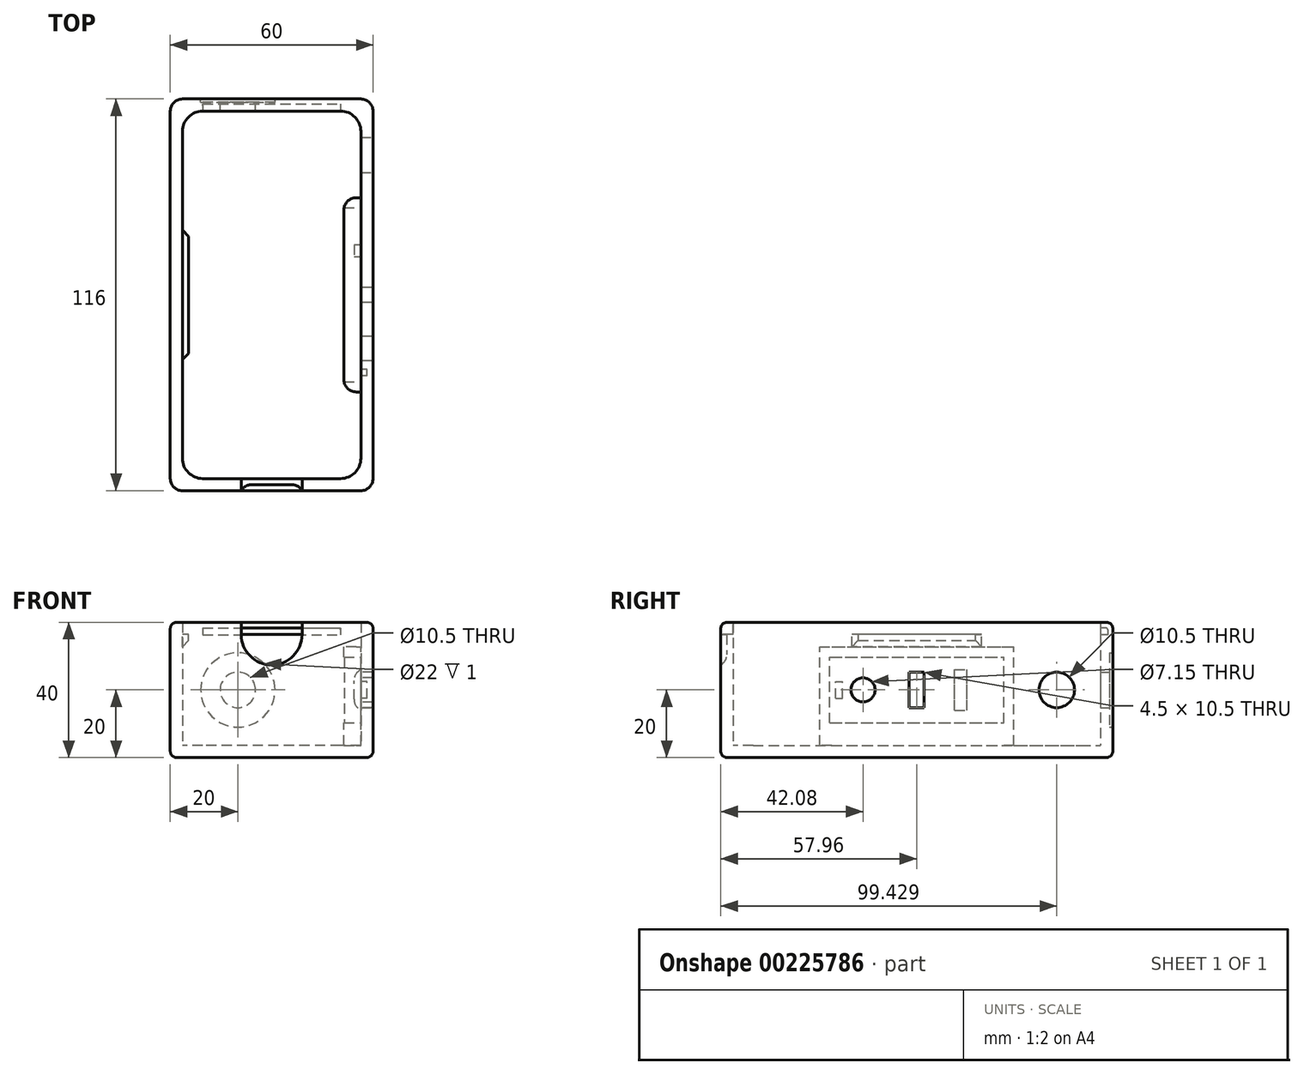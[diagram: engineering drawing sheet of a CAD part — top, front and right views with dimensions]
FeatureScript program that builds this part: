
annotation { "Feature Type Name" : "Feature", "Feature Type Description" : "" }
export const myFeature = defineFeature(function(context is Context, id is Id, definition is map)
    precondition{}
    {
        {
            assignVariable(context, id + "F0", {"name" : "O", "anyValue" : 3.6});
        }
        {
            assignVariable(context, id + "F1", {"name" : "H", "anyValue" : 40});
        }
        {
            var Q0;
            Q0=qCreatedBy(makeId("Top.planeOp"),FACE);
            var sketch = newSketch(context, id + "F2", { "sketchPlane" : qUnion([Q0])});
            skLineSegment(sketch, "E0.bottom", {"start": v(30, -58) * mm, "end": v(-30, -58) * mm});
            skLineSegment(sketch, "E0.top", {"start": v(30, 58) * mm, "end": v(-30, 58) * mm});
            skLineSegment(sketch, "E0.left", {"start": v(30, -58) * mm, "end": v(30, 58) * mm});
            skLineSegment(sketch, "E0.right", {"start": v(-30, -58) * mm, "end": v(-30, 58) * mm});
            skPoint(sketch, "E0.middle", {"position": v(0, 0) * mm});
            skLineSegment(sketch, "E1.0", {"start": v(26.4, 54.4) * mm, "end": v(-26.4, 54.4) * mm});
            skLineSegment(sketch, "E1.1", {"start": v(26.4, -54.4) * mm, "end": v(26.4, 54.4) * mm});
            skLineSegment(sketch, "E1.2", {"start": v(26.4, -54.4) * mm, "end": v(-26.4, -54.4) * mm});
            skLineSegment(sketch, "E1.3", {"start": v(-26.4, -54.4) * mm, "end": v(-26.4, 54.4) * mm});
            skSolve(sketch);
        }
        {
            var Q0;
            Q0=makeQuery(id+"F2.imprint","IMPRINT",FACE,{"disambiguationData":[TD([[makeQuery(id+"F2.imprint","IMPRINT",EDGE,{"derivedFrom":sQuery(id+"F2.wireOp",EDGE,"E0.bottom")}),-1.0]])]});
            extrude(context, id + "F3", {"entities" : qUnion([Q0]), "depth" : (getVariable(context, 'H')) * mm});
        }
        {
            var Q0;
            Q0=makeQuery(id+"F2.imprint","IMPRINT",FACE,{"disambiguationData":[TD([[makeQuery(id+"F2.imprint","IMPRINT",EDGE,{"derivedFrom":sQuery(id+"F2.wireOp",EDGE,"E1.0")}),1.0]])]});
            extrude(context, id + "F4", {"entities" : qUnion([Q0]), "operationType" : NewBodyOperationType.ADD, "depth" : (getVariable(context, 'O')) * mm});
        }
        {
            var Q0;
            Q0=makeQuery(id+"F3.opExtrude","SWEPT_FACE",FACE,{"disambiguationData":[OSD([sQuery(id+"F2.wireOp",EDGE,"E0.left")])]});
            var sketch = newSketch(context, id + "F5", { "sketchPlane" : qUnion([Q0])});
            skCircle(sketch, "E2", {"center": v(41.43, 20) * mm, "radius": 5.25 * mm});
            skSolve(sketch);
        }
        {
            var Q0;
            Q0=makeQuery(id+"F3.opExtrude","SWEPT_FACE",FACE,{"disambiguationData":[OSD([sQuery(id+"F2.wireOp",EDGE,"E0.top")])]});
            var sketch = newSketch(context, id + "F6", { "sketchPlane" : qUnion([Q0])});
            skCircle(sketch, "E3", {"center": v(10, 20) * mm, "radius": 5.25 * mm});
            skCircle(sketch, "E4", {"center": v(10, 20) * mm, "radius": 11 * mm});
            skSolve(sketch);
        }
        {
            var Q0;
            Q0=makeQuery(id+"F3.opExtrude","SWEPT_EDGE",EDGE,{"disambiguationData":[OSD([sQuery(id+"F2.wireOp",EDGE,"E0.top"),sQuery(id+"F2.wireOp",EDGE,"E0.left")])]});
            var Q1;
            Q1=makeQuery(id+"F3.opExtrude","SWEPT_EDGE",EDGE,{"disambiguationData":[OSD([sQuery(id+"F2.wireOp",EDGE,"E0.top"),sQuery(id+"F2.wireOp",EDGE,"E0.right")])]});
            var Q2;
            Q2=makeQuery(id+"F3.opExtrude","SWEPT_EDGE",EDGE,{"disambiguationData":[OSD([sQuery(id+"F2.wireOp",EDGE,"E0.bottom"),sQuery(id+"F2.wireOp",EDGE,"E0.right")])]});
            var Q3;
            Q3=makeQuery(id+"F3.opExtrude","SWEPT_EDGE",EDGE,{"disambiguationData":[OSD([sQuery(id+"F2.wireOp",EDGE,"E0.bottom"),sQuery(id+"F2.wireOp",EDGE,"E0.left")])]});
            fillet(context, id + "F7", {"entities" : qUnion([Q0, Q1, Q2, Q3]), "radius" : (getVariable(context, 'O')) * mm, "tangentPropagation" : true, "allowEdgeOverflow" : false});
        }
        {
            var Q0;
            Q0=makeQuery(id+"F3.opExtrude","SWEPT_EDGE",EDGE,{"disambiguationData":[OSD([sQuery(id+"F2.wireOp",EDGE,"E1.2"),sQuery(id+"F2.wireOp",EDGE,"E1.3")])]});
            var Q1;
            Q1=makeQuery(id+"F3.opExtrude","SWEPT_EDGE",EDGE,{"disambiguationData":[OSD([sQuery(id+"F2.wireOp",EDGE,"E1.1"),sQuery(id+"F2.wireOp",EDGE,"E1.2")])]});
            var Q2;
            Q2=makeQuery(id+"F3.opExtrude","SWEPT_EDGE",EDGE,{"disambiguationData":[OSD([sQuery(id+"F2.wireOp",EDGE,"E1.0"),sQuery(id+"F2.wireOp",EDGE,"E1.1")])]});
            var Q3;
            Q3=makeQuery(id+"F3.opExtrude","SWEPT_EDGE",EDGE,{"disambiguationData":[OSD([sQuery(id+"F2.wireOp",EDGE,"E1.0"),sQuery(id+"F2.wireOp",EDGE,"E1.3")])]});
            fillet(context, id + "F8", {"entities" : qUnion([Q0, Q1, Q2, Q3]), "radius" : (getVariable(context, 'O') * 1.67) * mm, "tangentPropagation" : true, "allowEdgeOverflow" : false});
        }
        {
            var Q0;
            Q0=makeQuery(id+"F6.imprint","IMPRINT",FACE,{"disambiguationData":[TD([[makeQuery(id+"F6.imprint","IMPRINT",EDGE,{"derivedFrom":sQuery(id+"F6.wireOp",EDGE,"E3")}),1.0]])]});
            extrude(context, id + "F9", {"entities" : qUnion([Q0]), "operationType" : NewBodyOperationType.REMOVE, "oppositeDirection" : true, "depth" : (getVariable(context, 'O')) * mm});
        }
        {
            var Q0;
            Q0=makeQuery(id+"F5.imprint","IMPRINT",FACE,{"disambiguationData":[TD([[makeQuery(id+"F5.imprint","IMPRINT",EDGE,{"derivedFrom":sQuery(id+"F5.wireOp",EDGE,"E2")}),1.0]])]});
            extrude(context, id + "F10", {"entities" : qUnion([Q0]), "operationType" : NewBodyOperationType.REMOVE, "oppositeDirection" : true, "depth" : (getVariable(context, 'O')) * mm});
        }
        {
            var Q0;
            Q0=makeQuery(id+"F3.opExtrude","SWEPT_FACE",FACE,{"disambiguationData":[OSD([sQuery(id+"F2.wireOp",EDGE,"E0.bottom")])]});
            var sketch = newSketch(context, id + "F11", { "sketchPlane" : qUnion([Q0])});
            skLineSegment(sketch, "E5.bottom", {"start": v(9, 36.4) * mm, "end": v(-9, 36.4) * mm});
            skLineSegment(sketch, "E5.top", {"start": v(9, 40) * mm, "end": v(-9, 40) * mm});
            skLineSegment(sketch, "E5.left", {"start": v(9, 36.4) * mm, "end": v(9, 40) * mm});
            skLineSegment(sketch, "E5.right", {"start": v(-9, 36.4) * mm, "end": v(-9, 40) * mm});
            skPoint(sketch, "E5.middle", {"position": v(0, 38.2) * mm});
            skPoint(sketch, "E5.middle.positionSnap0", {"position": v(0, 0) * mm});
            skPoint(sketch, "E5.centerSnap0", {"position": v(0, 0) * mm});
            skArc(sketch, "E6", {"start": v(-9, 36.4) * mm, "mid": v(0, 27.4) * mm, "end": v(9, 36.4) * mm});
            skSolve(sketch);
        }
        {
            var Q0;
            Q0=makeQuery(id+"F11.imprint","IMPRINT",FACE,{"disambiguationData":[TD([[makeQuery(id+"F11.imprint","IMPRINT",EDGE,{"derivedFrom":sQuery(id+"F11.wireOp",EDGE,"E5.bottom")}),-1.0]])]});
            extrude(context, id + "F12", {"entities" : qUnion([Q0]), "operationType" : NewBodyOperationType.REMOVE, "oppositeDirection" : true, "depth" : (getVariable(context, 'O')) * mm});
        }
        {
            var Q0;
            Q0=makeQuery(id+"F3.opExtrude","SWEPT_FACE",FACE,{"disambiguationData":[OSD([sQuery(id+"F2.wireOp",EDGE,"E1.0")])]});
            var sketch = newSketch(context, id + "F13", { "sketchPlane" : qUnion([Q0])});
            skLineSegment(sketch, "E7.bottom", {"start": v(-20.4, 38.3) * mm, "end": v(20.4, 38.3) * mm});
            skLineSegment(sketch, "E7.top", {"start": v(-20.4, 36.3) * mm, "end": v(20.4, 36.3) * mm});
            skLineSegment(sketch, "E7.left", {"start": v(-20.4, 38.3) * mm, "end": v(-20.4, 36.3) * mm});
            skLineSegment(sketch, "E7.right", {"start": v(20.4, 38.3) * mm, "end": v(20.4, 36.3) * mm});
            skSolve(sketch);
        }
        {
            var Q0;
            Q0=makeQuery(id+"F13.imprint","IMPRINT",FACE,{"disambiguationData":[TD([[makeQuery(id+"F13.imprint","IMPRINT",EDGE,{"derivedFrom":sQuery(id+"F13.wireOp",EDGE,"E7.bottom")}),-1.0]])]});
            extrude(context, id + "F14", {"entities" : qUnion([Q0]), "operationType" : NewBodyOperationType.REMOVE, "oppositeDirection" : true, "depth" : 2.1 * mm});
        }
        {
            var Q0;
            {var subQ0=sQuery(id+"F2.wireOp",EDGE,"E0.bottom");Q0=makeQuery(id+"F12.boolean.opBoolean","SPLIT",EDGE,{"disambiguationData":[TD([makeQuery(id+"F12.opExtrude","SWEPT_FACE",FACE,{"disambiguationData":[OSD([sQuery(id+"F11.wireOp",EDGE,"E5.left")])]})])],"derivedFrom":makeQuery(id+"F3.opExtrude","CAP_EDGE",EDGE,{"disambiguationData":[OSD([subQ0])],"isStart":false})});}
            var Q1;
            {var subQ0=sQuery(id+"F2.wireOp",EDGE,"E0.left");var subQ1=sQuery(id+"F2.wireOp",EDGE,"E0.bottom");Q1=makeQuery(id+"F7.opFillet","BLEND_EDGE",EDGE,{"blendedFrom":[makeQuery(id+"F3.opExtrude","SWEPT_EDGE",EDGE,{"disambiguationData":[OSD([subQ1,subQ0])]}),makeQuery(id+"F3.opExtrude","CAP_FACE",FACE,{"disambiguationData":[OSD([subQ1,sQuery(id+"F2.wireOp",EDGE,"E0.top"),subQ0,sQuery(id+"F2.wireOp",EDGE,"E0.right"),sQuery(id+"F2.wireOp",EDGE,"E1.0"),sQuery(id+"F2.wireOp",EDGE,"E1.1"),sQuery(id+"F2.wireOp",EDGE,"E1.2"),sQuery(id+"F2.wireOp",EDGE,"E1.3")])],"isStart":false})],"blendedInto":[makeQuery(id+"F3.opExtrude","CAP_FACE",FACE,{"disambiguationData":[OSD([subQ1,sQuery(id+"F2.wireOp",EDGE,"E0.top"),subQ0,sQuery(id+"F2.wireOp",EDGE,"E0.right"),sQuery(id+"F2.wireOp",EDGE,"E1.0"),sQuery(id+"F2.wireOp",EDGE,"E1.1"),sQuery(id+"F2.wireOp",EDGE,"E1.2"),sQuery(id+"F2.wireOp",EDGE,"E1.3")])],"isStart":false})]});}
            var Q2;
            Q2=makeQuery(id+"F3.opExtrude","CAP_EDGE",EDGE,{"disambiguationData":[OSD([sQuery(id+"F2.wireOp",EDGE,"E0.left")])],"isStart":false});
            var Q3;
            {var subQ0=sQuery(id+"F2.wireOp",EDGE,"E0.bottom");Q3=makeQuery(id+"F12.boolean.opBoolean","SPLIT",EDGE,{"disambiguationData":[TD([makeQuery(id+"F12.opExtrude","SWEPT_FACE",FACE,{"disambiguationData":[OSD([sQuery(id+"F11.wireOp",EDGE,"E5.right")])]})])],"derivedFrom":makeQuery(id+"F3.opExtrude","CAP_EDGE",EDGE,{"disambiguationData":[OSD([subQ0])],"isStart":false})});}
            var Q4;
            {var subQ0=sQuery(id+"F2.wireOp",EDGE,"E0.right");var subQ1=sQuery(id+"F2.wireOp",EDGE,"E0.bottom");Q4=makeQuery(id+"F7.opFillet","BLEND_EDGE",EDGE,{"blendedFrom":[makeQuery(id+"F3.opExtrude","SWEPT_EDGE",EDGE,{"disambiguationData":[OSD([subQ1,subQ0])]}),makeQuery(id+"F3.opExtrude","CAP_FACE",FACE,{"disambiguationData":[OSD([subQ1,sQuery(id+"F2.wireOp",EDGE,"E0.top"),sQuery(id+"F2.wireOp",EDGE,"E0.left"),subQ0,sQuery(id+"F2.wireOp",EDGE,"E1.0"),sQuery(id+"F2.wireOp",EDGE,"E1.1"),sQuery(id+"F2.wireOp",EDGE,"E1.2"),sQuery(id+"F2.wireOp",EDGE,"E1.3")])],"isStart":false})],"blendedInto":[makeQuery(id+"F3.opExtrude","CAP_FACE",FACE,{"disambiguationData":[OSD([subQ1,sQuery(id+"F2.wireOp",EDGE,"E0.top"),sQuery(id+"F2.wireOp",EDGE,"E0.left"),subQ0,sQuery(id+"F2.wireOp",EDGE,"E1.0"),sQuery(id+"F2.wireOp",EDGE,"E1.1"),sQuery(id+"F2.wireOp",EDGE,"E1.2"),sQuery(id+"F2.wireOp",EDGE,"E1.3")])],"isStart":false})]});}
            var Q5;
            Q5=makeQuery(id+"F3.opExtrude","CAP_EDGE",EDGE,{"disambiguationData":[OSD([sQuery(id+"F2.wireOp",EDGE,"E0.right")])],"isStart":false});
            var Q6;
            {var subQ0=sQuery(id+"F2.wireOp",EDGE,"E0.right");var subQ1=sQuery(id+"F2.wireOp",EDGE,"E0.top");Q6=makeQuery(id+"F7.opFillet","BLEND_EDGE",EDGE,{"blendedFrom":[makeQuery(id+"F3.opExtrude","SWEPT_EDGE",EDGE,{"disambiguationData":[OSD([subQ1,subQ0])]}),makeQuery(id+"F3.opExtrude","CAP_FACE",FACE,{"disambiguationData":[OSD([sQuery(id+"F2.wireOp",EDGE,"E0.bottom"),subQ1,sQuery(id+"F2.wireOp",EDGE,"E0.left"),subQ0,sQuery(id+"F2.wireOp",EDGE,"E1.0"),sQuery(id+"F2.wireOp",EDGE,"E1.1"),sQuery(id+"F2.wireOp",EDGE,"E1.2"),sQuery(id+"F2.wireOp",EDGE,"E1.3")])],"isStart":false})],"blendedInto":[makeQuery(id+"F3.opExtrude","CAP_FACE",FACE,{"disambiguationData":[OSD([sQuery(id+"F2.wireOp",EDGE,"E0.bottom"),subQ1,sQuery(id+"F2.wireOp",EDGE,"E0.left"),subQ0,sQuery(id+"F2.wireOp",EDGE,"E1.0"),sQuery(id+"F2.wireOp",EDGE,"E1.1"),sQuery(id+"F2.wireOp",EDGE,"E1.2"),sQuery(id+"F2.wireOp",EDGE,"E1.3")])],"isStart":false})]});}
            var Q7;
            Q7=makeQuery(id+"F3.opExtrude","CAP_EDGE",EDGE,{"disambiguationData":[OSD([sQuery(id+"F2.wireOp",EDGE,"E0.top")])],"isStart":false});
            var Q8;
            {var subQ0=sQuery(id+"F2.wireOp",EDGE,"E0.left");var subQ1=sQuery(id+"F2.wireOp",EDGE,"E0.top");Q8=makeQuery(id+"F7.opFillet","BLEND_EDGE",EDGE,{"blendedFrom":[makeQuery(id+"F3.opExtrude","SWEPT_EDGE",EDGE,{"disambiguationData":[OSD([subQ1,subQ0])]}),makeQuery(id+"F3.opExtrude","CAP_FACE",FACE,{"disambiguationData":[OSD([sQuery(id+"F2.wireOp",EDGE,"E0.bottom"),subQ1,subQ0,sQuery(id+"F2.wireOp",EDGE,"E0.right"),sQuery(id+"F2.wireOp",EDGE,"E1.0"),sQuery(id+"F2.wireOp",EDGE,"E1.1"),sQuery(id+"F2.wireOp",EDGE,"E1.2"),sQuery(id+"F2.wireOp",EDGE,"E1.3")])],"isStart":false})],"blendedInto":[makeQuery(id+"F3.opExtrude","CAP_FACE",FACE,{"disambiguationData":[OSD([sQuery(id+"F2.wireOp",EDGE,"E0.bottom"),subQ1,subQ0,sQuery(id+"F2.wireOp",EDGE,"E0.right"),sQuery(id+"F2.wireOp",EDGE,"E1.0"),sQuery(id+"F2.wireOp",EDGE,"E1.1"),sQuery(id+"F2.wireOp",EDGE,"E1.2"),sQuery(id+"F2.wireOp",EDGE,"E1.3")])],"isStart":false})]});}
            fillet(context, id + "F15", {"entities" : qUnion([Q0, Q1, Q2, Q3, Q4, Q5, Q6, Q7, Q8]), "radius" : (getVariable(context, 'O') / 2) * mm, "tangentPropagation" : true, "allowEdgeOverflow" : false});
        }
        {
            var Q0;
            {var subQ0=sQuery(id+"F2.wireOp",EDGE,"E1.3");var subQ1=sQuery(id+"F2.wireOp",EDGE,"E1.2");var subQ2=sQuery(id+"F2.wireOp",EDGE,"E1.1");var subQ3=sQuery(id+"F2.wireOp",EDGE,"E1.0");Q0=makeQuery(id+"F4.boolean.opBoolean","MERGE",FACE,{"derivedFrom":[makeQuery(id+"F3.opExtrude","CAP_FACE",FACE,{"disambiguationData":[OSD([sQuery(id+"F2.wireOp",EDGE,"E0.bottom"),sQuery(id+"F2.wireOp",EDGE,"E0.top"),sQuery(id+"F2.wireOp",EDGE,"E0.left"),sQuery(id+"F2.wireOp",EDGE,"E0.right"),subQ3,subQ2,subQ1,subQ0])],"isStart":true}),makeQuery(id+"F4.opExtrude","CAP_FACE",FACE,{"disambiguationData":[OSD([subQ3,subQ2,subQ1,subQ0])],"isStart":true})]});}
            fillet(context, id + "F16", {"entities" : qUnion([Q0]), "radius" : (getVariable(context, 'O') / 2) * mm, "tangentPropagation" : true, "allowEdgeOverflow" : false});
        }
        {
            var Q0;
            Q0=makeQuery(id+"F6.imprint","IMPRINT",FACE,{"disambiguationData":[TD([[makeQuery(id+"F6.imprint","IMPRINT",EDGE,{"derivedFrom":sQuery(id+"F6.wireOp",EDGE,"E3")}),-1.0]])]});
            extrude(context, id + "F17", {"entities" : qUnion([Q0]), "operationType" : NewBodyOperationType.REMOVE, "oppositeDirection" : true, "depth" : 1 * mm});
        }
        {
            var Q0;
            Q0=makeQuery(id+"F14.boolean.opBoolean","COPY",EDGE,{"derivedFrom":makeQuery(id+"F14.opExtrude","CAP_EDGE",EDGE,{"disambiguationData":[OSD([sQuery(id+"F13.wireOp",EDGE,"E7.bottom")])],"isStart":false})});
            fillet(context, id + "F18", {"entities" : qUnion([Q0]), "radius" : 0.5 * mm, "tangentPropagation" : true, "allowEdgeOverflow" : false});
        }
        {
            var Q0;
            Q0=makeQuery(id+"F3.opExtrude","SWEPT_FACE",FACE,{"disambiguationData":[OSD([sQuery(id+"F2.wireOp",EDGE,"E1.1")])]});
            var sketch = newSketch(context, id + "F19", { "sketchPlane" : qUnion([Q0])});
            skLineSegment(sketch, "E8.bottom", {"start": v(25, 11) * mm, "end": v(-25, 11) * mm});
            skLineSegment(sketch, "E8.top", {"start": v(25, 29) * mm, "end": v(-25, 29) * mm});
            skLineSegment(sketch, "E8.left", {"start": v(25, 11) * mm, "end": v(25, 29) * mm});
            skLineSegment(sketch, "E8.right", {"start": v(-25, 11) * mm, "end": v(-25, 29) * mm});
            skPoint(sketch, "E8.middle", {"position": v(0, 20) * mm});
            skLineSegment(sketch, "E9.bottom", {"start": v(2.29, 14.75) * mm, "end": v(-2.21, 14.75) * mm});
            skLineSegment(sketch, "E9.top", {"start": v(2.29, 25.25) * mm, "end": v(-2.21, 25.25) * mm});
            skLineSegment(sketch, "E9.left", {"start": v(2.29, 14.75) * mm, "end": v(2.29, 25.25) * mm});
            skLineSegment(sketch, "E9.right", {"start": v(-2.21, 14.75) * mm, "end": v(-2.21, 25.25) * mm});
            skPoint(sketch, "E9.middle", {"position": v(0.04, 20) * mm});
            skCircle(sketch, "E10", {"center": v(15.92, 20) * mm, "radius": 3.58 * mm});
            skLineSegment(sketch, "E11.bottom", {"start": v(-11.2, 14) * mm, "end": v(-14.8, 14) * mm});
            skLineSegment(sketch, "E11.top", {"start": v(-11.2, 26) * mm, "end": v(-14.8, 26) * mm});
            skLineSegment(sketch, "E11.left", {"start": v(-11.2, 14) * mm, "end": v(-11.2, 26) * mm});
            skLineSegment(sketch, "E11.right", {"start": v(-14.8, 14) * mm, "end": v(-14.8, 26) * mm});
            skPoint(sketch, "E11.middle", {"position": v(-13, 20) * mm});
            skPoint(sketch, "E11.middle.positionSnap0", {"position": v(-25, 20) * mm});
            skPoint(sketch, "E11.centerSnap0", {"position": v(-25, 20) * mm});
            skLineSegment(sketch, "E12.bottom", {"start": v(24.02, 17.5) * mm, "end": v(22.02, 17.5) * mm});
            skLineSegment(sketch, "E12.top", {"start": v(24.02, 22.5) * mm, "end": v(22.02, 22.5) * mm});
            skLineSegment(sketch, "E12.left", {"start": v(24.02, 17.5) * mm, "end": v(24.02, 22.5) * mm});
            skLineSegment(sketch, "E12.right", {"start": v(22.02, 17.5) * mm, "end": v(22.02, 22.5) * mm});
            skPoint(sketch, "E12.middle", {"position": v(23.02, 20) * mm});
            skLineSegment(sketch, "E13.0", {"start": v(25.75, 29.75) * mm, "end": v(-25.75, 29.75) * mm});
            skLineSegment(sketch, "E13.1", {"start": v(25.75, 10.25) * mm, "end": v(25.75, 29.75) * mm});
            skLineSegment(sketch, "E13.2", {"start": v(25.75, 10.25) * mm, "end": v(-25.75, 10.25) * mm});
            skLineSegment(sketch, "E13.3", {"start": v(-25.75, 10.25) * mm, "end": v(-25.75, 29.75) * mm});
            skLineSegment(sketch, "E14.0", {"start": v(28.75, 32.75) * mm, "end": v(-28.75, 32.75) * mm});
            skLineSegment(sketch, "E14.1", {"start": v(28.75, 7.25) * mm, "end": v(28.75, 32.75) * mm});
            skLineSegment(sketch, "E14.2", {"start": v(28.75, 7.25) * mm, "end": v(-28.75, 7.25) * mm});
            skLineSegment(sketch, "E14.3", {"start": v(-28.75, 7.25) * mm, "end": v(-28.75, 32.75) * mm});
            skLineSegment(sketch, "E15", {"start": v(-28.75, 7.25) * mm, "end": v(-28.75, 3.6) * mm});
            skLineSegment(sketch, "E16", {"start": v(28.75, 7.25) * mm, "end": v(28.75, 3.6) * mm});
            skLineSegment(sketch, "E17.bottom", {"start": v(-28.75, 32.75) * mm, "end": v(28.75, 32.75) * mm});
            skLineSegment(sketch, "E17.top", {"start": v(-28.75, 36.4) * mm, "end": v(28.75, 36.4) * mm});
            skLineSegment(sketch, "E17.left", {"start": v(-28.75, 32.75) * mm, "end": v(-28.75, 36.4) * mm});
            skLineSegment(sketch, "E17.right", {"start": v(28.75, 32.75) * mm, "end": v(28.75, 36.4) * mm});
            skSolve(sketch);
        }
        {
            var Q0;
            Q0=makeQuery(id+"F3.opExtrude","SWEPT_FACE",FACE,{"disambiguationData":[OSD([sQuery(id+"F2.wireOp",EDGE,"E1.3")])]});
            var sketch = newSketch(context, id + "F20", { "sketchPlane" : qUnion([Q0])});
            skLineSegment(sketch, "E18.bottom", {"start": v(19.14, 32.8) * mm, "end": v(-19.14, 32.8) * mm});
            skLineSegment(sketch, "E18.top", {"start": v(19.14, 36.4) * mm, "end": v(-19.14, 36.4) * mm});
            skLineSegment(sketch, "E18.left", {"start": v(19.14, 32.8) * mm, "end": v(19.14, 36.4) * mm});
            skLineSegment(sketch, "E18.right", {"start": v(-19.14, 32.8) * mm, "end": v(-19.14, 36.4) * mm});
            skPoint(sketch, "E18.middle", {"position": v(0, 34.6) * mm});
            skSolve(sketch);
        }
        {
            var Q0;
            Q0=makeQuery(id+"F3.opExtrude","SWEPT_FACE",FACE,{"disambiguationData":[OSD([sQuery(id+"F2.wireOp",EDGE,"E0.right")])]});
            var sketch = newSketch(context, id + "F21", { "sketchPlane" : qUnion([Q0])});
            skText(sketch, "E19", { "text": "zerø", "fontName": "RobotoSlab-Regular.ttf"});
            skLineSegment(sketch, "E20", {"start": v(3.6, 30.14) * mm, "end": v(3.6, 38.2) * mm});
            skLineSegment(sketch, "E21", {"start": v(3.6, 9.86) * mm, "end": v(3.6, 1.8) * mm});
            const initialGuessF21  = {"E19": [-0.0244, 0.0062, 1, 0, 0.01958]};
            skSetInitialGuess(sketch, initialGuessF21);
            skSolve(sketch);
        }
        {
            var Q0;
            Q0=makeQuery(id+"F3.opExtrude","SWEPT_FACE",FACE,{"disambiguationData":[OSD([sQuery(id+"F2.wireOp",EDGE,"E1.2")])]});
            var sketch = newSketch(context, id + "F22", { "sketchPlane" : qUnion([Q0])});
            skLineSegment(sketch, "E22", {"start": v(-9, 38.4) * mm, "end": v(-20.4, 38.4) * mm});
            skLineSegment(sketch, "E23", {"start": v(9, 38.4) * mm, "end": v(20.4, 38.4) * mm});
            skLineSegment(sketch, "E24", {"start": v(9, 36.4) * mm, "end": v(20.4, 36.4) * mm});
            skLineSegment(sketch, "E25", {"start": v(-9, 36.4) * mm, "end": v(-20.4, 36.4) * mm});
            skSolve(sketch);
        }
        {
            var Q0;
            Q0=makeQuery(id+"F11.imprint","IMPRINT",FACE,{"disambiguationData":[TD([[makeQuery(id+"F11.imprint","IMPRINT",EDGE,{"derivedFrom":sQuery(id+"F11.wireOp",EDGE,"E5.bottom")}),1.0]])]});
            extrude(context, id + "F23", {"entities" : qUnion([Q0]), "operationType" : NewBodyOperationType.REMOVE, "oppositeDirection" : true, "depth" : (getVariable(context, 'O') / 2) * mm});
        }
        {
            var Q0;
            Q0=makeQuery(id+"F20.imprint","IMPRINT",FACE,{"disambiguationData":[TD([[makeQuery(id+"F20.imprint","IMPRINT",EDGE,{"derivedFrom":sQuery(id+"F20.wireOp",EDGE,"E18.bottom")}),-1.0]])]});
            extrude(context, id + "F24", {"entities" : qUnion([Q0]), "operationType" : NewBodyOperationType.ADD, "depth" : (getVariable(context, 'O') * .5) * mm});
        }
        {
            var Q0;
            Q0=makeQuery(id+"F24.opExtrude","CAP_EDGE",EDGE,{"disambiguationData":[OSD([sQuery(id+"F20.wireOp",EDGE,"E18.right")])],"isStart":false});
            var Q1;
            Q1=makeQuery(id+"F24.opExtrude","CAP_EDGE",EDGE,{"disambiguationData":[OSD([sQuery(id+"F20.wireOp",EDGE,"E18.bottom")])],"isStart":false});
            var Q2;
            Q2=makeQuery(id+"F24.opExtrude","CAP_EDGE",EDGE,{"disambiguationData":[OSD([sQuery(id+"F20.wireOp",EDGE,"E18.left")])],"isStart":false});
            var Q3;
            Q3=makeQuery(id+"FUkj4zLFzn2cjNl_1.opExtrude","CAP_EDGE",EDGE,{"disambiguationData":[OSD([sQuery(id+"F19.wireOp",EDGE,"Uwhg5jXr-3Yt5-poT9-xr3U-90L54EeIlBer.right")])],"isStart":false});
            var Q4;
            Q4=makeQuery(id+"FUkj4zLFzn2cjNl_1.opExtrude","CAP_EDGE",EDGE,{"disambiguationData":[OSD([sQuery(id+"F19.wireOp",EDGE,"Uwhg5jXr-3Yt5-poT9-xr3U-90L54EeIlBer.left")])],"isStart":false});
            var Q5;
            Q5=makeQuery(id+"FUkj4zLFzn2cjNl_1.opExtrude","CAP_EDGE",EDGE,{"disambiguationData":[OSD([sQuery(id+"F19.wireOp",EDGE,"Uwhg5jXr-3Yt5-poT9-xr3U-90L54EeIlBer.bottom")])],"isStart":false});
            chamfer(context, id + "F25", {"entities" : qUnion([Q0, Q1, Q2, Q3, Q4, Q5]), "width" : (getVariable(context, 'O') * 0.5) * mm, "tangentPropagation" : true});
        }
        {
            var Q0;
            Q0=makeQuery(id+"F19.imprint","IMPRINT",FACE,{"disambiguationData":[TD([[makeQuery(id+"F19.imprint","IMPRINT",EDGE,{"derivedFrom":sQuery(id+"F19.wireOp",EDGE,"E9.bottom")}),-1.0]])]});
            var Q1;
            Q1=makeQuery(id+"F19.imprint","IMPRINT",FACE,{"disambiguationData":[TD([[makeQuery(id+"F19.imprint","IMPRINT",EDGE,{"derivedFrom":sQuery(id+"F19.wireOp",EDGE,"E10")}),1.0]])]});
            extrude(context, id + "F26", {"entities" : qUnion([Q0, Q1]), "operationType" : NewBodyOperationType.REMOVE, "endBound" : BoundingType.THROUGH_ALL, "oppositeDirection" : true, "depth" : 25 * mm});
        }
        {
            var Q0;
            Q0=makeQuery(id+"F19.imprint","IMPRINT",FACE,{"disambiguationData":[TD([[makeQuery(id+"F19.imprint","IMPRINT",EDGE,{"derivedFrom":sQuery(id+"F19.wireOp",EDGE,"E12.bottom")}),-1.0]])]});
            extrude(context, id + "F27", {"entities" : qUnion([Q0]), "operationType" : NewBodyOperationType.REMOVE, "oppositeDirection" : true, "depth" : (getVariable(context, 'O') * 0.5) * mm});
        }
        {
            var Q0;
            Q0=makeQuery(id+"F19.imprint","IMPRINT",FACE,{"disambiguationData":[TD([[makeQuery(id+"F19.imprint","IMPRINT",EDGE,{"derivedFrom":sQuery(id+"F19.wireOp",EDGE,"E11.bottom")}),-1.0]])]});
            extrude(context, id + "F28", {"entities" : qUnion([Q0]), "operationType" : NewBodyOperationType.ADD, "depth" : 2 * mm});
        }
        {
            var Q0;
            Q0=makeQuery(id+"F19.imprint","IMPRINT",FACE,{"disambiguationData":[TD([[makeQuery(id+"F19.imprint","IMPRINT",EDGE,{"derivedFrom":sQuery(id+"F19.wireOp",EDGE,"E13.0")}),-1.0]])]});
            var Q1;
            Q1=makeQuery(id+"F19.imprint","IMPRINT",FACE,{"disambiguationData":[TD([[makeQuery(id+"F19.imprint","IMPRINT",EDGE,{"derivedFrom":sQuery(id+"F19.wireOp",EDGE,"E14.2")}),1.0]])]});
            var Q2;
            Q2=makeQuery(id+"F19.imprint","IMPRINT",FACE,{"disambiguationData":[TD([[makeQuery(id+"F19.imprint","IMPRINT",EDGE,{"derivedFrom":sQuery(id+"F19.wireOp",EDGE,"E17.bottom")}),1.0]])]});
            extrude(context, id + "F29", {"entities" : qUnion([Q0, Q1, Q2]), "operationType" : NewBodyOperationType.ADD, "depth" : 5 * mm});
        }
        {
            var Q0;
            Q0=makeQuery(id+"F29.opExtrude","CAP_EDGE",EDGE,{"disambiguationData":[OSD([sQuery(id+"F19.wireOp",EDGE,"E14.3"),sQuery(id+"F19.wireOp",EDGE,"E15"),sQuery(id+"F19.wireOp",EDGE,"E17.left")])],"isStart":false});
            var Q1;
            Q1=makeQuery(id+"F29.opExtrude","CAP_EDGE",EDGE,{"disambiguationData":[OSD([sQuery(id+"F19.wireOp",EDGE,"E17.top")])],"isStart":false});
            var Q2;
            Q2=makeQuery(id+"F29.opExtrude","CAP_EDGE",EDGE,{"disambiguationData":[OSD([sQuery(id+"F19.wireOp",EDGE,"E14.1"),sQuery(id+"F19.wireOp",EDGE,"E16"),sQuery(id+"F19.wireOp",EDGE,"E17.right")])],"isStart":false});
            var Q3;
            Q3=makeQuery(id+"F28.opExtrude","CAP_EDGE",EDGE,{"disambiguationData":[OSD([sQuery(id+"F19.wireOp",EDGE,"E11.top")])],"isStart":false});
            var Q4;
            Q4=makeQuery(id+"F28.opExtrude","CAP_EDGE",EDGE,{"disambiguationData":[OSD([sQuery(id+"F19.wireOp",EDGE,"E11.bottom")])],"isStart":false});
            var Q5;
            Q5=makeQuery(id+"F29.opExtrude","CAP_EDGE",EDGE,{"disambiguationData":[OSD([sQuery(id+"F19.wireOp",EDGE,"E13.2")])],"isStart":true});
            var Q6;
            Q6=makeQuery(id+"F29.opExtrude","CAP_EDGE",EDGE,{"disambiguationData":[OSD([sQuery(id+"F19.wireOp",EDGE,"E13.0")])],"isStart":true});
            fillet(context, id + "F30", {"entities" : qUnion([Q0, Q1, Q2, Q3, Q4, Q5, Q6]), "radius" : (getVariable(context, 'O')) * mm, "tangentPropagation" : true, "allowEdgeOverflow" : false});
        }
        {
            var Q0;
            Q0=makeQuery(id+"F23.boolean.opBoolean","COPY",EDGE,{"derivedFrom":makeQuery(id+"F23.opExtrude","CAP_EDGE",EDGE,{"disambiguationData":[OSD([sQuery(id+"F11.wireOp",EDGE,"E6")])],"isStart":false})});
            fillet(context, id + "F31", {"entities" : qUnion([Q0]), "radius" : (getVariable(context, 'O')) * mm, "tangentPropagation" : true, "allowEdgeOverflow" : false});
        }
    });
